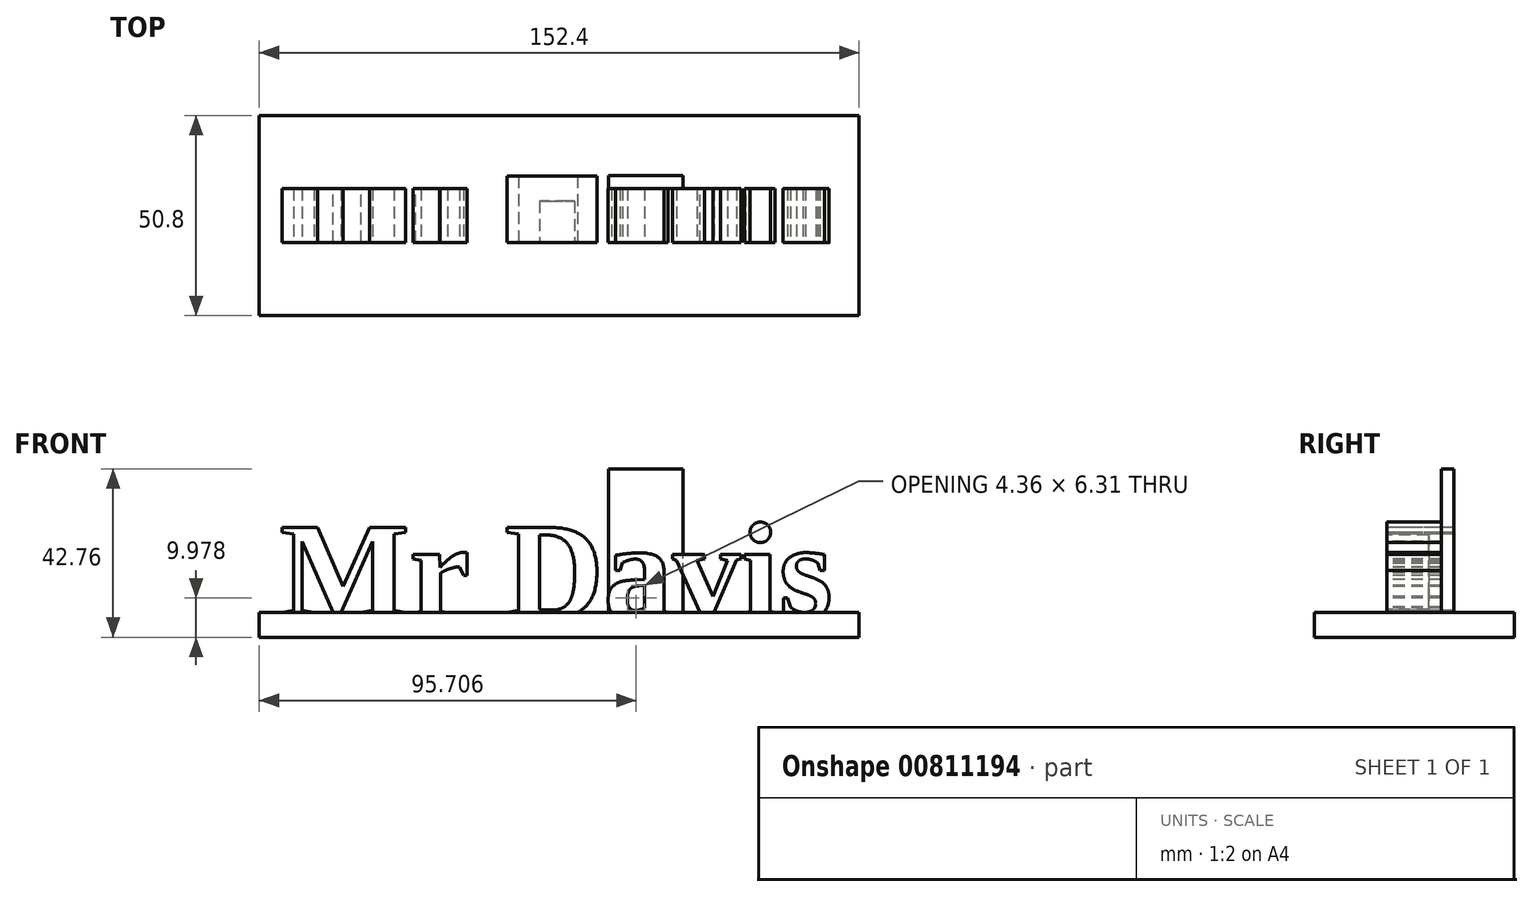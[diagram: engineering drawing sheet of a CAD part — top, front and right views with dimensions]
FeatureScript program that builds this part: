
annotation { "Feature Type Name" : "Feature", "Feature Type Description" : "" }
export const myFeature = defineFeature(function(context is Context, id is Id, definition is map)
    precondition{}
    {
        {
            var Q0;
            Q0=qCreatedBy(makeId("Top.planeOp"),FACE);
            var sketch = newSketch(context, id + "F0", { "sketchPlane" : qUnion([Q0])});
            skLineSegment(sketch, "E0.bottom", {"start": v(76.2, 25.4) * mm, "end": v(-76.2, 25.4) * mm});
            skLineSegment(sketch, "E0.top", {"start": v(76.2, -25.4) * mm, "end": v(-76.2, -25.4) * mm});
            skLineSegment(sketch, "E0.left", {"start": v(76.2, 25.4) * mm, "end": v(76.2, -25.4) * mm});
            skLineSegment(sketch, "E0.right", {"start": v(-76.2, 25.4) * mm, "end": v(-76.2, -25.4) * mm});
            skPoint(sketch, "E0.middle", {"position": v(0, 0) * mm});
            skSolve(sketch);
        }
        {
            var Q0;
            Q0 = qSketchRegion(id + "F0", true);
            extrude(context, id + "F1", {"entities" : qUnion([Q0]), "depth" : 6.35 * mm, "offsetDistance" : 25.4 * mm});
        }
        {
            var Q0;
            Q0=qCreatedBy(makeId("Front.planeOp"),FACE);
            var sketch = newSketch(context, id + "F2", { "sketchPlane" : qUnion([Q0])});
            skText(sketch, "E1", { "text": "Mr Davis", "fontName": "Tinos-Bold.ttf"});
            const initialGuessF2  = {"E1": [-0.07097, 0.0051, 1, 0, 0.0251]};
            skSetInitialGuess(sketch, initialGuessF2);
            skSolve(sketch);
        }
        {
            var Q0;
            Q0 = qSketchRegion(id + "F2", true);
            extrude(context, id + "F3", {"entities" : qUnion([Q0]), "operationType" : NewBodyOperationType.ADD, "oppositeDirection" : true, "depth" : 13.72 * mm, "offsetDistance" : 25.4 * mm, "symmetric" : true});
        }
        {
            var Q0;
            Q0=makeQuery(id+"F3.opExtrude","CAP_FACE",FACE,{"disambiguationData":[OSD([sQuery(id+"F2.wireOp",EDGE,"E1.sketch_text.stroke-44"),sQuery(id+"F2.wireOp",EDGE,"E1.sketch_text.stroke-45"),sQuery(id+"F2.wireOp",EDGE,"E1.sketch_text.stroke-46"),sQuery(id+"F2.wireOp",EDGE,"E1.sketch_text.stroke-47"),sQuery(id+"F2.wireOp",EDGE,"E1.sketch_text.stroke-48"),sQuery(id+"F2.wireOp",EDGE,"E1.sketch_text.stroke-49"),sQuery(id+"F2.wireOp",EDGE,"E1.sketch_text.stroke-50"),sQuery(id+"F2.wireOp",EDGE,"E1.sketch_text.stroke-51"),sQuery(id+"F2.wireOp",EDGE,"E1.sketch_text.stroke-52"),sQuery(id+"F2.wireOp",EDGE,"E1.sketch_text.stroke-53"),sQuery(id+"F2.wireOp",EDGE,"E1.sketch_text.stroke-54"),sQuery(id+"F2.wireOp",EDGE,"E1.sketch_text.stroke-55"),sQuery(id+"F2.wireOp",EDGE,"E1.sketch_text.stroke-56"),sQuery(id+"F2.wireOp",EDGE,"E1.sketch_text.stroke-57"),sQuery(id+"F2.wireOp",EDGE,"E1.sketch_text.stroke-58"),sQuery(id+"F2.wireOp",EDGE,"E1.sketch_text.stroke-59"),sQuery(id+"F2.wireOp",EDGE,"E1.sketch_text.stroke-60"),sQuery(id+"F2.wireOp",EDGE,"E1.sketch_text.stroke-61"),sQuery(id+"F2.wireOp",EDGE,"E1.sketch_text.stroke-62"),sQuery(id+"F2.wireOp",EDGE,"E1.sketch_text.stroke-63")])],"isStart":false});
            var sketch = newSketch(context, id + "F4", { "sketchPlane" : qUnion([Q0])});
            skLineSegment(sketch, "E2.bottom", {"start": v(27.36, 6.26) * mm, "end": v(-31.48, 6.26) * mm});
            skLineSegment(sketch, "E2.top", {"start": v(27.36, 42.76) * mm, "end": v(-31.48, 42.76) * mm});
            skLineSegment(sketch, "E2.left", {"start": v(27.36, 6.26) * mm, "end": v(27.36, 42.76) * mm});
            skLineSegment(sketch, "E2.right", {"start": v(-31.48, 6.26) * mm, "end": v(-31.48, 42.76) * mm});
            skPoint(sketch, "E2.middle", {"position": v(-2.06, 24.51) * mm});
            skLineSegment(sketch, "E3.bottom", {"start": v(-31.48, 42.76) * mm, "end": v(-12.57, 42.76) * mm});
            skLineSegment(sketch, "E3.top", {"start": v(-31.48, 6.26) * mm, "end": v(-12.57, 6.26) * mm});
            skLineSegment(sketch, "E3.left", {"start": v(-31.48, 42.76) * mm, "end": v(-31.48, 6.26) * mm});
            skLineSegment(sketch, "E3.right", {"start": v(-12.57, 42.76) * mm, "end": v(-12.57, 6.26) * mm});
            skLineSegment(sketch, "E4.bottom", {"start": v(27.36, 42.76) * mm, "end": v(7.7, 42.76) * mm});
            skLineSegment(sketch, "E4.top", {"start": v(27.36, 6.26) * mm, "end": v(7.7, 6.26) * mm});
            skLineSegment(sketch, "E4.left", {"start": v(27.36, 42.76) * mm, "end": v(27.36, 6.26) * mm});
            skLineSegment(sketch, "E4.right", {"start": v(7.7, 42.76) * mm, "end": v(7.7, 6.26) * mm});
            skSolve(sketch);
        }
        {
            var Q0;
            Q0=makeQuery(id+"F4.imprint","IMPRINT",FACE,{"disambiguationData":[TD([[makeQuery(id+"F4.imprint","IMPRINT",EDGE,{"derivedFrom":sQuery(id+"F4.wireOp",EDGE,"E4.bottom")}),1.0]])]});
            var Q1;
            Q1=makeQuery(id+"F4.imprint","IMPRINT",FACE,{"disambiguationData":[TD([[makeQuery(id+"F4.imprint","IMPRINT",EDGE,{"derivedFrom":makeQuery(id+"F3.opExtrude","CAP_EDGE",EDGE,{"disambiguationData":[OSD([sQuery(id+"F2.wireOp",EDGE,"E1.sketch_text.stroke-44")])],"isStart":false})}),-1.0]])]});
            extrude(context, id + "F5", {"entities" : qUnion([Q0, Q1]), "depth" : 6.35 * mm, "offsetDistance" : 25.4 * mm, "symmetric" : true});
        }
        {
            var Q0;
            Q0=makeQuery(id+"F4.imprint","IMPRINT",FACE,{"disambiguationData":[TD([[makeQuery(id+"F4.imprint","IMPRINT",EDGE,{"derivedFrom":sQuery(id+"F4.wireOp",EDGE,"E3.bottom")}),-1.0]])]});
            var Q1;
            {var subQ16=sQuery(id+"F2.wireOp",EDGE,"E1.sketch_text.stroke-44");Q1=makeQuery(id+"F4.imprint","IMPRINT",FACE,{"disambiguationData":[TD([[makeQuery(id+"F4.imprint","IMPRINT",EDGE,{"derivedFrom":makeQuery(id+"F3.opExtrude","CAP_EDGE",EDGE,{"disambiguationData":[OSD([subQ16])],"isStart":false})}),1.0]])]});}
            var Q2;
            {var subQ1=sQuery(id+"F2.wireOp",EDGE,"E1.sketch_text.stroke-60");Q2=makeQuery(id+"F4.imprint","IMPRINT",FACE,{"disambiguationData":[TD([[makeQuery(id+"F4.imprint","IMPRINT",EDGE,{"derivedFrom":makeQuery(id+"F3.opExtrude","CAP_EDGE",EDGE,{"disambiguationData":[OSD([subQ1])],"isStart":false})}),1.0]])]});}
            extrude(context, id + "F6", {"entities" : qUnion([Q0, Q1, Q2]), "operationType" : NewBodyOperationType.ADD, "depth" : 6.35 * mm, "offsetDistance" : 25.4 * mm, "symmetric" : true});
        }
        {
            var Q0;
            Q0=makeQuery(id+"F4.imprint","IMPRINT",FACE,{"disambiguationData":[TD([[makeQuery(id+"F4.imprint","IMPRINT",EDGE,{"derivedFrom":sQuery(id+"F4.wireOp",EDGE,"E2.bottom")}),-1.0]])]});
            var Q1;
            Q1=makeQuery(id+"F1.opExtrude","SWEPT_BODY",BODY,{"disambiguationData":[OSD([sQuery(id+"F0.wireOp",EDGE,"E0.bottom"),sQuery(id+"F0.wireOp",EDGE,"E0.top"),sQuery(id+"F0.wireOp",EDGE,"E0.left"),sQuery(id+"F0.wireOp",EDGE,"E0.right")])]});
            extrude(context, id + "F7", {"entities" : qUnion([Q0]), "depth" : 3.3 * mm, "endBoundEntityBody" : qUnion([Q1]), "offsetDistance" : 25.4 * mm});
        }
        {
            var Q0;
            Q0=makeQuery(id+"F4.imprint","IMPRINT",FACE,{"disambiguationData":[TD([[makeQuery(id+"F4.imprint","IMPRINT",EDGE,{"derivedFrom":makeQuery(id+"F3.opExtrude","CAP_EDGE",EDGE,{"disambiguationData":[OSD([sQuery(id+"F2.wireOp",EDGE,"E1.sketch_text.stroke-44")])],"isStart":false})}),-1.0]])]});
            extrude(context, id + "F8", {"entities" : qUnion([Q0]), "operationType" : NewBodyOperationType.ADD, "oppositeDirection" : true, "depth" : 2.8 * mm, "offsetDistance" : 25.4 * mm});
        }
    });
